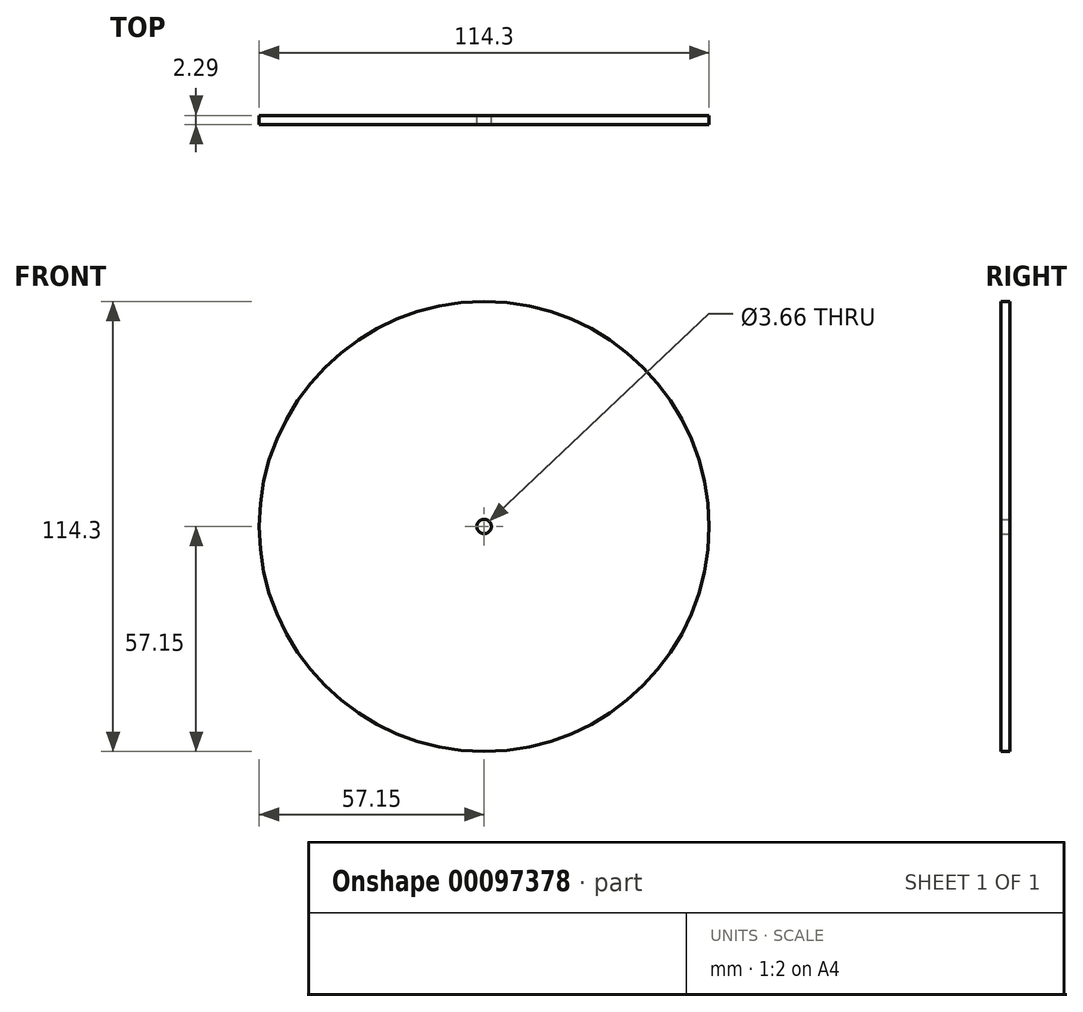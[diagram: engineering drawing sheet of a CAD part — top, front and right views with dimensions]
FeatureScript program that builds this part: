
annotation { "Feature Type Name" : "Feature", "Feature Type Description" : "" }
export const myFeature = defineFeature(function(context is Context, id is Id, definition is map)
    precondition{}
    {
        {
            var Q0;
            Q0=qCreatedBy(makeId("Front.planeOp"),FACE);
            var sketch = newSketch(context, id + "F0", { "sketchPlane" : qUnion([Q0])});
            skCircle(sketch, "E0", {"center": v(0, 0) * mm, "radius": 57.15 * mm});
            skSolve(sketch);
        }
        {
            var Q0;
            Q0=makeQuery(id+"F0.imprint","IMPRINT",FACE,{"disambiguationData":[TD([[makeQuery(id+"F0.imprint","IMPRINT",EDGE,{"derivedFrom":sQuery(id+"F0.wireOp",EDGE,"E0")}),1.0]])]});
            extrude(context, id + "F1", {"entities" : qUnion([Q0]), "depth" : 2.3 * mm});
        }
        {
            var Q0;
            Q0=sQuery(id+"F0.wireOp",VERTEX,"E0.center");
            var Q1;
            Q1=makeQuery(id+"F1.opExtrude","SWEPT_BODY",BODY,{"disambiguationData":[OSD([sQuery(id+"F0.wireOp",EDGE,"E0")])]});
            hole(context, id + "F2", {"style" : HoleStyle.SIMPLE, "endStyle" : HoleEndStyle.THROUGH, "oppositeDirection" : true, "standardTappedOrClearance" : lookupTablePath({ "standard" : "ANSI", "fit" : "Close", "size" : "#6", "type" : "Clearance" }), "standardBlindInLast" : lookupTablePath({ "fit" : "Close", "standard" : "ANSI", "size" : "#6", "type" : "Clearance" }), "holeDiameter" : 3.66 * mm, "locations" : qUnion([Q0]), "scope" : qUnion([Q1]), "isTappedThrough" : true});
        }
    });
